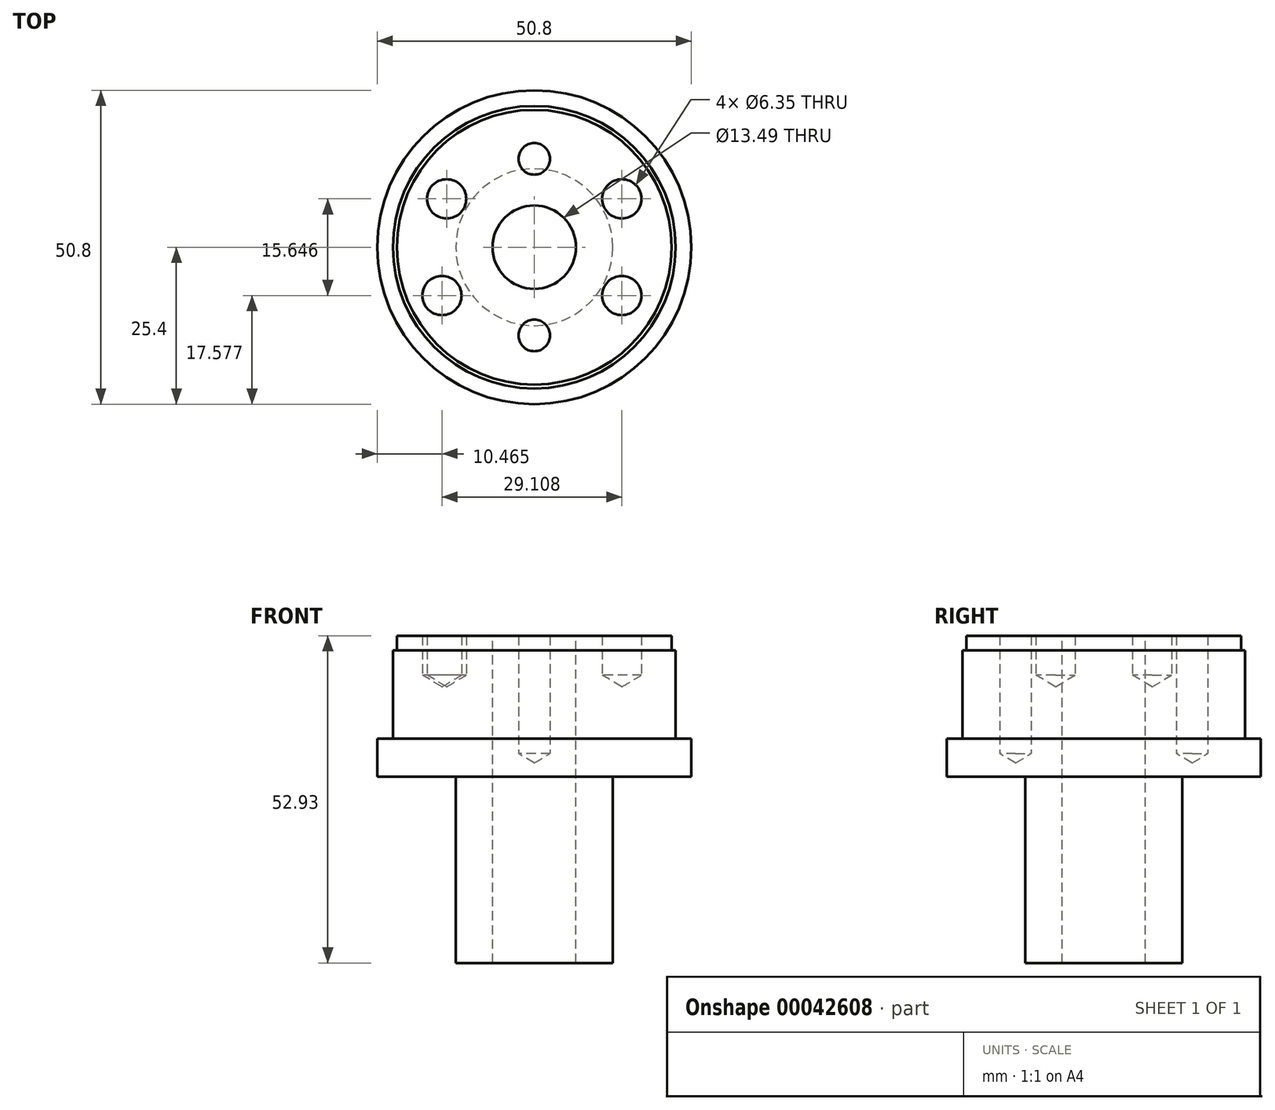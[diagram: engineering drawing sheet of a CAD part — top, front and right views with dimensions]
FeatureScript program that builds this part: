
annotation { "Feature Type Name" : "Feature", "Feature Type Description" : "" }
export const myFeature = defineFeature(function(context is Context, id is Id, definition is map)
    precondition{}
    {
        {
            var Q0;
            Q0=qCreatedBy(makeId("Front.planeOp"),FACE);
            var sketch = newSketch(context, id + "F0", { "sketchPlane" : qUnion([Q0])});
            skLineSegment(sketch, "E0", {"start": v(0, 0) * mm, "end": v(0, 52.93) * mm});
            skLineSegment(sketch, "E1", {"start": v(0, 0) * mm, "end": v(12.7, 0) * mm});
            skLineSegment(sketch, "E2", {"start": v(12.7, 0) * mm, "end": v(12.7, 30.16) * mm});
            skLineSegment(sketch, "E3", {"start": v(12.7, 30.16) * mm, "end": v(25.4, 30.16) * mm});
            skLineSegment(sketch, "E4", {"start": v(25.4, 30.16) * mm, "end": v(25.4, 36.27) * mm});
            skLineSegment(sketch, "E5", {"start": v(25.4, 36.27) * mm, "end": v(22.86, 36.27) * mm});
            skLineSegment(sketch, "E6", {"start": v(22.86, 36.27) * mm, "end": v(22.86, 50.56) * mm});
            skLineSegment(sketch, "E7", {"start": v(22.86, 50.56) * mm, "end": v(22.23, 50.56) * mm});
            skLineSegment(sketch, "E8", {"start": v(22.23, 50.56) * mm, "end": v(22.23, 52.93) * mm});
            skLineSegment(sketch, "E9", {"start": v(22.23, 52.93) * mm, "end": v(0, 52.93) * mm});
            skSolve(sketch);
        }
        {
            var Q0;
            Q0=makeQuery(id+"F0.imprint","IMPRINT",FACE,{"disambiguationData":[TD([[makeQuery(id+"F0.imprint","IMPRINT",EDGE,{"derivedFrom":sQuery(id+"F0.wireOp",EDGE,"E0")}),-1.0]])]});
            var Q1;
            Q1=sQuery(id+"F0.wireOp",EDGE,"E0");
            revolve(context, id + "F1", {"entities" : qUnion([Q0]), "axis" : qUnion([Q1]), "revolveType" : RevolveType.FULL});
        }
        {
            var Q0;
            Q0=qCreatedBy(makeId("Top.planeOp"),FACE);
            var sketch = newSketch(context, id + "F2", { "sketchPlane" : qUnion([Q0])});
            skPoint(sketch, "E10", {"position": v(0, 0) * mm});
            skSolve(sketch);
        }
        {
            var Q0;
            Q0=sQuery(id+"F2.wireOp",VERTEX,"E10");
            var Q1;
            Q1=makeQuery(id+"F1.opRevolve","SWEPT_BODY",BODY,{"disambiguationData":[OSD([sQuery(id+"F0.wireOp",EDGE,"E0"),sQuery(id+"F0.wireOp",EDGE,"E1"),sQuery(id+"F0.wireOp",EDGE,"E2"),sQuery(id+"F0.wireOp",EDGE,"E3"),sQuery(id+"F0.wireOp",EDGE,"E4"),sQuery(id+"F0.wireOp",EDGE,"E5"),sQuery(id+"F0.wireOp",EDGE,"E6"),sQuery(id+"F0.wireOp",EDGE,"E7"),sQuery(id+"F0.wireOp",EDGE,"E8"),sQuery(id+"F0.wireOp",EDGE,"E9")])]});
            hole(context, id + "F3", {"style" : HoleStyle.SIMPLE, "holeDiameter" : 13.5 * mm, "endStyle" : HoleEndStyle.THROUGH, "oppositeDirection" : true, "locations" : qUnion([Q0]), "scope" : qUnion([Q1])});
        }
        {
            var Q0;
            Q0=qCreatedBy(makeId("Top.planeOp"),FACE);
            cPlane(context, id + "F4", {"entities" : qUnion([Q0]), "cplaneType" : CPlaneType.OFFSET, "offset" : 52.93 * mm, "width" : 152.4 * mm, "height" : 152.4 * mm});
        }
        {
            var Q0;
            Q0=qCreatedBy(id+"F4.planeOp",FACE);
            var sketch = newSketch(context, id + "F5", { "sketchPlane" : qUnion([Q0])});
            skPoint(sketch, "E11", {"position": v(-14.17, 7.82) * mm});
            skPoint(sketch, "E12", {"position": v(14.17, 7.82) * mm});
            skSolve(sketch);
        }
        {
            var Q0;
            Q0=sQuery(id+"F5.wireOp",VERTEX,"E11");
            var Q1;
            Q1=sQuery(id+"F5.wireOp",VERTEX,"E12");
            var Q2;
            Q2=makeQuery(id+"F1.opRevolve","SWEPT_BODY",BODY,{"disambiguationData":[OSD([sQuery(id+"F0.wireOp",EDGE,"E0"),sQuery(id+"F0.wireOp",EDGE,"E1"),sQuery(id+"F0.wireOp",EDGE,"E2"),sQuery(id+"F0.wireOp",EDGE,"E3"),sQuery(id+"F0.wireOp",EDGE,"E4"),sQuery(id+"F0.wireOp",EDGE,"E5"),sQuery(id+"F0.wireOp",EDGE,"E6"),sQuery(id+"F0.wireOp",EDGE,"E7"),sQuery(id+"F0.wireOp",EDGE,"E8"),sQuery(id+"F0.wireOp",EDGE,"E9")])]});
            hole(context, id + "F6", {"style" : HoleStyle.SIMPLE, "holeDiameter" : 6.35 * mm, "endStyle" : HoleEndStyle.BLIND, "holeDepth" : 6.35 * mm, "locations" : qUnion([Q0, Q1]), "scope" : qUnion([Q2])});
        }
        {
            var Q0;
            Q0=qCreatedBy(id+"F4.planeOp",FACE);
            var sketch = newSketch(context, id + "F7", { "sketchPlane" : qUnion([Q0])});
            skPoint(sketch, "E13", {"position": v(14.17, -7.82) * mm});
            skPoint(sketch, "E14", {"position": v(-14.94, -7.82) * mm});
            skSolve(sketch);
        }
        {
            var Q0;
            Q0=sQuery(id+"F7.wireOp",VERTEX,"E14");
            var Q1;
            Q1=sQuery(id+"F7.wireOp",VERTEX,"E13");
            var Q2;
            Q2=makeQuery(id+"F1.opRevolve","SWEPT_BODY",BODY,{"disambiguationData":[OSD([sQuery(id+"F0.wireOp",EDGE,"E0"),sQuery(id+"F0.wireOp",EDGE,"E1"),sQuery(id+"F0.wireOp",EDGE,"E2"),sQuery(id+"F0.wireOp",EDGE,"E3"),sQuery(id+"F0.wireOp",EDGE,"E4"),sQuery(id+"F0.wireOp",EDGE,"E5"),sQuery(id+"F0.wireOp",EDGE,"E6"),sQuery(id+"F0.wireOp",EDGE,"E7"),sQuery(id+"F0.wireOp",EDGE,"E8"),sQuery(id+"F0.wireOp",EDGE,"E9")])]});
            hole(context, id + "F8", {"style" : HoleStyle.SIMPLE, "holeDiameter" : 6.35 * mm, "endStyle" : HoleEndStyle.BLIND, "holeDepth" : 6.35 * mm, "locations" : qUnion([Q0, Q1]), "scope" : qUnion([Q2])});
        }
        {
            var Q0;
            Q0=qCreatedBy(id+"F4.planeOp",FACE);
            var sketch = newSketch(context, id + "F9", { "sketchPlane" : qUnion([Q0])});
            skPoint(sketch, "E15", {"position": v(0, -14.29) * mm});
            skPoint(sketch, "E16", {"position": v(0, 14.29) * mm});
            skSolve(sketch);
        }
        {
            var Q0;
            Q0=sQuery(id+"F9.wireOp",VERTEX,"E15");
            var Q1;
            Q1=sQuery(id+"F9.wireOp",VERTEX,"E16");
            var Q2;
            Q2=makeQuery(id+"F1.opRevolve","SWEPT_BODY",BODY,{"disambiguationData":[OSD([sQuery(id+"F0.wireOp",EDGE,"E0"),sQuery(id+"F0.wireOp",EDGE,"E1"),sQuery(id+"F0.wireOp",EDGE,"E2"),sQuery(id+"F0.wireOp",EDGE,"E3"),sQuery(id+"F0.wireOp",EDGE,"E4"),sQuery(id+"F0.wireOp",EDGE,"E5"),sQuery(id+"F0.wireOp",EDGE,"E6"),sQuery(id+"F0.wireOp",EDGE,"E7"),sQuery(id+"F0.wireOp",EDGE,"E8"),sQuery(id+"F0.wireOp",EDGE,"E9")])]});
            hole(context, id + "F10", {"style" : HoleStyle.SIMPLE, "holeDiameter" : 5.1 * mm, "endStyle" : HoleEndStyle.BLIND, "holeDepth" : 19.05 * mm, "locations" : qUnion([Q0, Q1]), "scope" : qUnion([Q2])});
        }
    });
